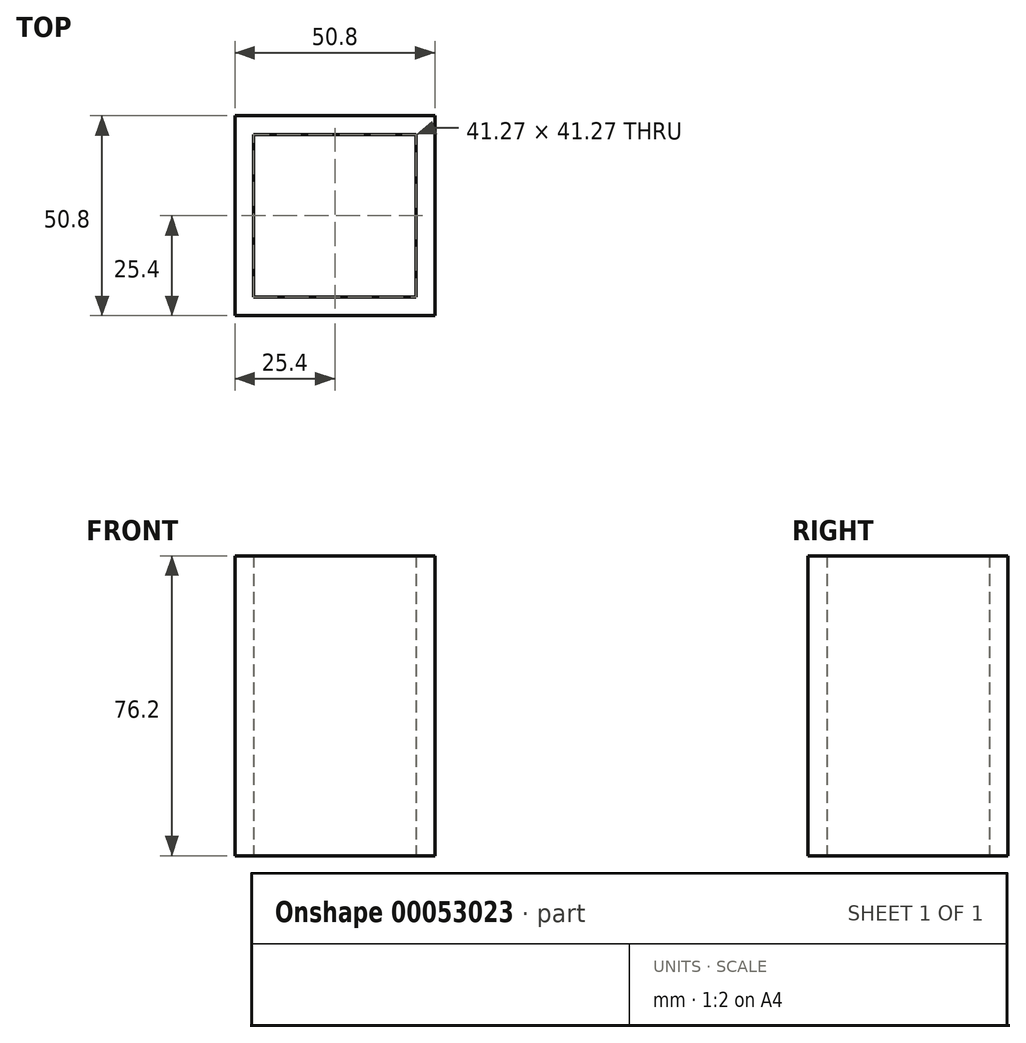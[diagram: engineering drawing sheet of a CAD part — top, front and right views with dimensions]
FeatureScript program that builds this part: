
annotation { "Feature Type Name" : "Feature", "Feature Type Description" : "" }
export const myFeature = defineFeature(function(context is Context, id is Id, definition is map)
    precondition{}
    {
        {
            var Q0;
            Q0=qCreatedBy(makeId("Top.planeOp"),FACE);
            var sketch = newSketch(context, id + "F0", { "sketchPlane" : qUnion([Q0])});
            skLineSegment(sketch, "E0.bottom", {"start": v(0, 0) * mm, "end": v(-50.8, 0) * mm});
            skLineSegment(sketch, "E0.top", {"start": v(0, 50.8) * mm, "end": v(-50.8, 50.8) * mm});
            skLineSegment(sketch, "E0.left", {"start": v(0, 0) * mm, "end": v(0, 50.8) * mm});
            skLineSegment(sketch, "E0.right", {"start": v(-50.8, 0) * mm, "end": v(-50.8, 50.8) * mm});
            skLineSegment(sketch, "E1.bottom", {"start": v(-4.76, 4.76) * mm, "end": v(-46.04, 4.76) * mm});
            skLineSegment(sketch, "E1.top", {"start": v(-4.76, 46.04) * mm, "end": v(-46.04, 46.04) * mm});
            skLineSegment(sketch, "E1.left", {"start": v(-4.76, 4.76) * mm, "end": v(-4.76, 46.04) * mm});
            skLineSegment(sketch, "E1.right", {"start": v(-46.04, 4.76) * mm, "end": v(-46.04, 46.04) * mm});
            skSolve(sketch);
        }
        {
            var Q0;
            Q0=makeQuery(id+"F0.imprint","IMPRINT",FACE,{"disambiguationData":[TD([[makeQuery(id+"F0.imprint","IMPRINT",EDGE,{"derivedFrom":sQuery(id+"F0.wireOp",EDGE,"E0.bottom")}),-1.0]])]});
            extrude(context, id + "F1", {"entities" : qUnion([Q0]), "depth" : 76.2 * mm});
        }
    });
